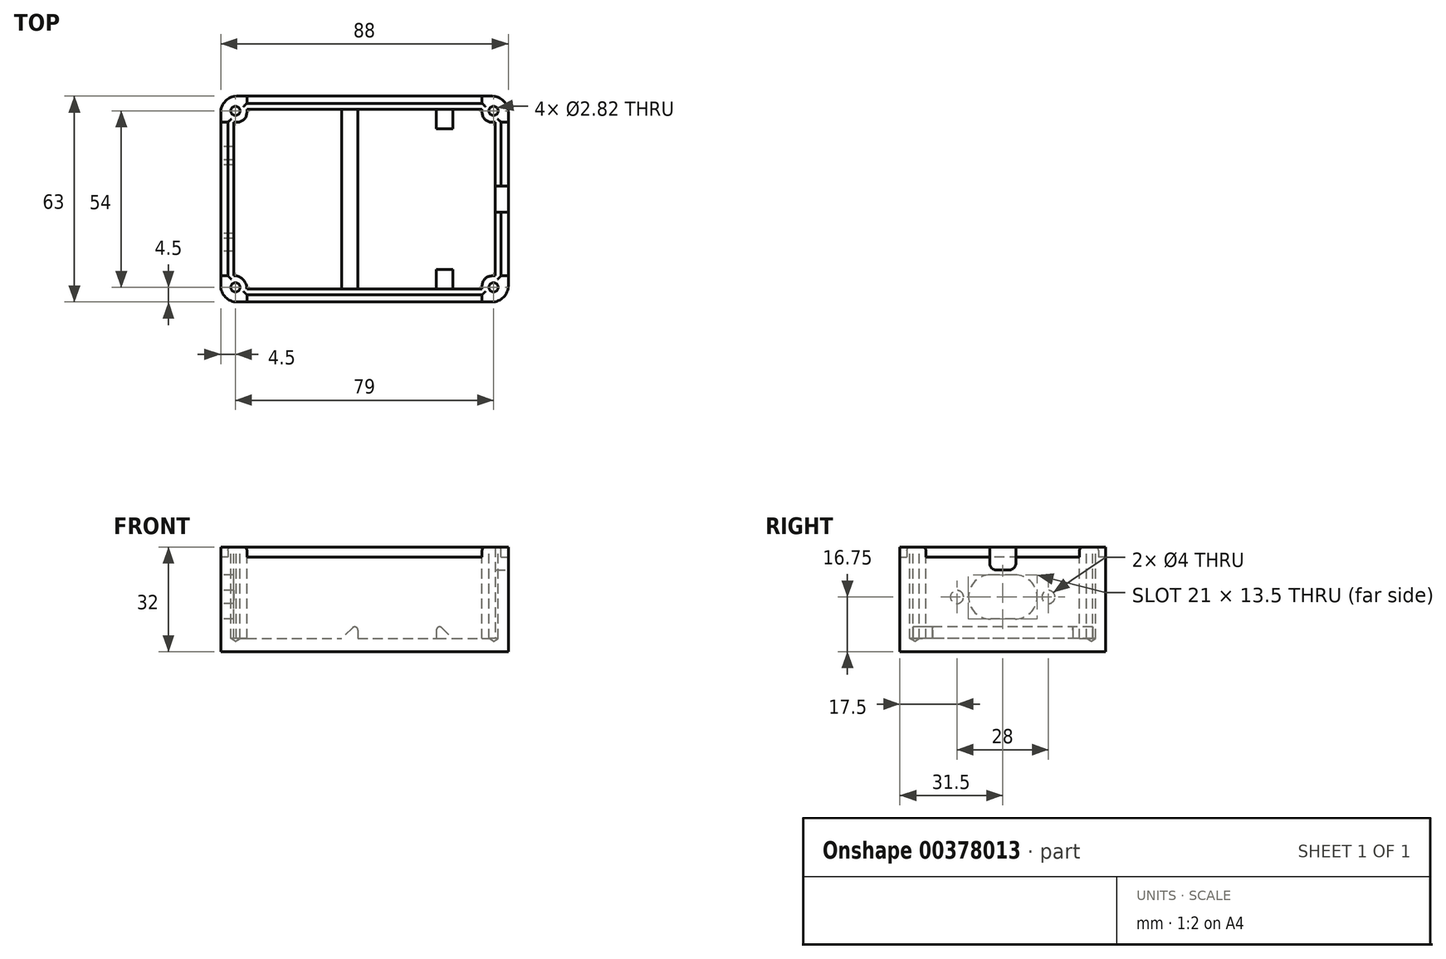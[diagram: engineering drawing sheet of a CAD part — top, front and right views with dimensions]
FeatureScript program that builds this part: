
annotation { "Feature Type Name" : "Feature", "Feature Type Description" : "" }
export const myFeature = defineFeature(function(context is Context, id is Id, definition is map)
    precondition{}
    {
        {
            var Q0;
            Q0=qCreatedBy(makeId("Top.planeOp"),FACE);
            cPlane(context, id + "F0", {"entities" : qUnion([Q0]), "cplaneType" : CPlaneType.OFFSET, "offset" : 25 * mm, "width" : 150 * mm, "height" : 150 * mm});
        }
        {
            var Q0;
            Q0=qCreatedBy(makeId("Top.planeOp"),FACE);
            var sketch = newSketch(context, id + "F1", { "sketchPlane" : qUnion([Q0])});
            skLineSegment(sketch, "E0.bottom", {"start": v(-80, 0) * mm, "end": v(0, 0) * mm});
            skLineSegment(sketch, "E0.top", {"start": v(-80, -55) * mm, "end": v(0, -55) * mm});
            skLineSegment(sketch, "E0.left", {"start": v(-80, 0) * mm, "end": v(-80, -55) * mm});
            skLineSegment(sketch, "E0.right", {"start": v(0, 0) * mm, "end": v(0, -55) * mm});
            skSolve(sketch);
        }
        {
            var Q0;
            Q0=makeQuery(id+"F1.imprint","IMPRINT",FACE,{"disambiguationData":[TD([[makeQuery(id+"F1.imprint","IMPRINT",EDGE,{"derivedFrom":sQuery(id+"F1.wireOp",EDGE,"E0.bottom")}),-1.0]])]});
            extrude(context, id + "F2", {"entities" : qUnion([Q0]), "depth" : 25 * mm});
        }
        {
            var Q0;
            Q0=makeQuery(id+"F2.opExtrude","CAP_FACE",FACE,{"disambiguationData":[OSD([sQuery(id+"F1.wireOp",EDGE,"E0.bottom"),sQuery(id+"F1.wireOp",EDGE,"E0.top"),sQuery(id+"F1.wireOp",EDGE,"E0.left"),sQuery(id+"F1.wireOp",EDGE,"E0.right")])],"isStart":false});
            shell(context, id + "F3", {"entities" : qUnion([Q0]), "thickness" : 4 * mm, "oppositeDirection" : true});
        }
        {
            var Q0;
            Q0=makeQuery(id+"F3.opShell","OFFSET_FACE",FACE,{"disambiguationData":[OSD([sQuery(id+"F1.wireOp",EDGE,"E0.bottom"),sQuery(id+"F1.wireOp",EDGE,"E0.top"),sQuery(id+"F1.wireOp",EDGE,"E0.left"),sQuery(id+"F1.wireOp",EDGE,"E0.right")])]});
            var sketch = newSketch(context, id + "F4", { "sketchPlane" : qUnion([Q0])});
            skLineSegment(sketch, "E1.bottom", {"start": v(-47, 0) * mm, "end": v(-42, 0) * mm});
            skLineSegment(sketch, "E1.top", {"start": v(-47, -55) * mm, "end": v(-42, -55) * mm});
            skLineSegment(sketch, "E1.left", {"start": v(-47, 0) * mm, "end": v(-47, -55) * mm});
            skLineSegment(sketch, "E1.right", {"start": v(-42, 0) * mm, "end": v(-42, -55) * mm});
            skSolve(sketch);
        }
        {
            var Q0;
            Q0 = qSketchRegion(id + "F4", true);
            extrude(context, id + "F5", {"entities" : qUnion([Q0]), "operationType" : NewBodyOperationType.ADD, "depth" : 5 * mm});
        }
        {
            var Q0;
            {var subQ0=sQuery(id+"F1.wireOp",EDGE,"E0.bottom");var subQ1=sQuery(id+"F1.wireOp",EDGE,"E0.top");var subQ2=sQuery(id+"F1.wireOp",EDGE,"E0.right");Q0=makeQuery(id+"F5.boolean.opBoolean","SPLIT",FACE,{"disambiguationData":[TD([makeQuery(id+"F3.opShell","OFFSET_FACE",FACE,{"disambiguationData":[OSD([subQ2])]})])],"derivedFrom":makeQuery(id+"F3.opShell","OFFSET_FACE",FACE,{"disambiguationData":[OSD([subQ0,subQ1,sQuery(id+"F1.wireOp",EDGE,"E0.left"),subQ2])]})});}
            var sketch = newSketch(context, id + "F6", { "sketchPlane" : qUnion([Q0])});
            skLineSegment(sketch, "E2.bottom", {"start": v(-18, 0) * mm, "end": v(-13, 0) * mm});
            skLineSegment(sketch, "E2.top", {"start": v(-18, -6) * mm, "end": v(-13, -6) * mm});
            skLineSegment(sketch, "E2.left", {"start": v(-18, 0) * mm, "end": v(-18, -6) * mm});
            skLineSegment(sketch, "E2.right", {"start": v(-13, 0) * mm, "end": v(-13, -6) * mm});
            skLineSegment(sketch, "E3.bottom", {"start": v(-18, -49) * mm, "end": v(-13, -49) * mm});
            skLineSegment(sketch, "E3.top", {"start": v(-18, -55) * mm, "end": v(-13, -55) * mm});
            skLineSegment(sketch, "E3.left", {"start": v(-18, -49) * mm, "end": v(-18, -55) * mm});
            skLineSegment(sketch, "E3.right", {"start": v(-13, -49) * mm, "end": v(-13, -55) * mm});
            skSolve(sketch);
        }
        {
            var Q0;
            Q0 = qSketchRegion(id + "F6", true);
            extrude(context, id + "F7", {"entities" : qUnion([Q0]), "operationType" : NewBodyOperationType.ADD, "depth" : 5 * mm});
        }
        {
            var Q0;
            Q0=qCreatedBy(id+"F0.planeOp",FACE);
            var sketch = newSketch(context, id + "F8", { "sketchPlane" : qUnion([Q0])});
            skLineSegment(sketch, "E4.bottom", {"start": v(-80, 0) * mm, "end": v(0, 0) * mm});
            skLineSegment(sketch, "E4.top", {"start": v(-80, -55) * mm, "end": v(0, -55) * mm});
            skLineSegment(sketch, "E4.left", {"start": v(-80, 0) * mm, "end": v(-80, -55) * mm});
            skLineSegment(sketch, "E4.right", {"start": v(0, 0) * mm, "end": v(0, -55) * mm});
            skLineSegment(sketch, "E5.bottom", {"start": v(-81.8, 1.8) * mm, "end": v(1.8, 1.8) * mm});
            skLineSegment(sketch, "E5.top", {"start": v(-81.8, -56.8) * mm, "end": v(1.8, -56.8) * mm});
            skLineSegment(sketch, "E5.left", {"start": v(-81.8, 1.8) * mm, "end": v(-81.8, -56.8) * mm});
            skLineSegment(sketch, "E5.right", {"start": v(1.8, 1.8) * mm, "end": v(1.8, -56.8) * mm});
            skSolve(sketch);
        }
        {
            var Q0;
            Q0 = qSketchRegion(id + "F8", true);
            extrude(context, id + "F9", {"entities" : qUnion([Q0]), "operationType" : NewBodyOperationType.ADD, "depth" : 3 * mm});
        }
        {
            var Q0;
            Q0=qCreatedBy(id+"F0.planeOp",FACE);
            var sketch = newSketch(context, id + "F10", { "sketchPlane" : qUnion([Q0])});
            skLineSegment(sketch, "E6", {"start": v(-79, -4) * mm, "end": v(-84, -4) * mm});
            skLineSegment(sketch, "E7", {"start": v(-84, -4) * mm, "end": v(-84, 4) * mm});
            skLineSegment(sketch, "E8", {"start": v(-84, 4) * mm, "end": v(-76, 4) * mm});
            skLineSegment(sketch, "E9", {"start": v(-76, 4) * mm, "end": v(-76, -1) * mm});
            skArc(sketch, "E10", {"start": v(-79, -4) * mm, "mid": v(-76.88, -3.12) * mm, "end": v(-76, -1) * mm});
            skLineSegment(sketch, "E11", {"start": v(-1, -4) * mm, "end": v(4, -4) * mm});
            skLineSegment(sketch, "E12", {"start": v(4, -4) * mm, "end": v(4, 4) * mm});
            skLineSegment(sketch, "E13", {"start": v(4, 4) * mm, "end": v(-4, 4) * mm});
            skLineSegment(sketch, "E14", {"start": v(-4, 4) * mm, "end": v(-4, -1) * mm});
            skLineSegment(sketch, "E15", {"start": v(-4, -54) * mm, "end": v(-4, -59) * mm});
            skLineSegment(sketch, "E16", {"start": v(-4, -59) * mm, "end": v(4, -59) * mm});
            skLineSegment(sketch, "E17", {"start": v(4, -59) * mm, "end": v(4, -51) * mm});
            skLineSegment(sketch, "E18", {"start": v(4, -51) * mm, "end": v(-1, -51) * mm});
            skArc(sketch, "E19", {"start": v(-1, -51) * mm, "mid": v(-3.12, -51.88) * mm, "end": v(-4, -54) * mm});
            skLineSegment(sketch, "E20", {"start": v(-79.19, -51) * mm, "end": v(-84, -51) * mm});
            skLineSegment(sketch, "E21", {"start": v(-84, -51) * mm, "end": v(-84, -59) * mm});
            skLineSegment(sketch, "E22", {"start": v(-84, -59) * mm, "end": v(-76, -59) * mm});
            skLineSegment(sketch, "E23", {"start": v(-76, -59) * mm, "end": v(-76, -55) * mm});
            skArc(sketch, "E24", {"start": v(-76, -55) * mm, "mid": v(-76.9, -52.44) * mm, "end": v(-79.19, -51) * mm});
            skArc(sketch, "E25", {"start": v(-4, -1) * mm, "mid": v(-3.12, -3.12) * mm, "end": v(-1, -4) * mm});
            skSolve(sketch);
        }
        {
            var Q0;
            Q0 = qSketchRegion(id + "F10", true);
            extrude(context, id + "F11", {"entities" : qUnion([Q0]), "operationType" : NewBodyOperationType.ADD, "oppositeDirection" : true, "depth" : 25 * mm});
        }
        {
            var Q0;
            Q0 = qSketchRegion(id + "F10", true);
            extrude(context, id + "F12", {"entities" : qUnion([Q0]), "operationType" : NewBodyOperationType.ADD, "depth" : 3 * mm});
        }
        {
            var Q0;
            Q0=makeQuery(id+"F12.boolean.opBoolean","MERGE",FACE,{"derivedFrom":[makeQuery(id+"F9.opExtrude","CAP_FACE",FACE,{"disambiguationData":[OSD([sQuery(id+"F8.wireOp",EDGE,"E4.bottom"),sQuery(id+"F8.wireOp",EDGE,"E4.top"),sQuery(id+"F8.wireOp",EDGE,"E4.left"),sQuery(id+"F8.wireOp",EDGE,"E4.right"),sQuery(id+"F8.wireOp",EDGE,"E5.bottom"),sQuery(id+"F8.wireOp",EDGE,"E5.top"),sQuery(id+"F8.wireOp",EDGE,"E5.left"),sQuery(id+"F8.wireOp",EDGE,"E5.right")])],"isStart":false}),makeQuery(id+"F12.opExtrude","CAP_FACE",FACE,{"disambiguationData":[OSD([sQuery(id+"F10.wireOp",EDGE,"E6"),sQuery(id+"F10.wireOp",EDGE,"E7"),sQuery(id+"F10.wireOp",EDGE,"E8"),sQuery(id+"F10.wireOp",EDGE,"E9"),sQuery(id+"F10.wireOp",EDGE,"E10")])],"isStart":false}),makeQuery(id+"F12.opExtrude","CAP_FACE",FACE,{"disambiguationData":[OSD([sQuery(id+"F10.wireOp",EDGE,"E11"),sQuery(id+"F10.wireOp",EDGE,"E12"),sQuery(id+"F10.wireOp",EDGE,"E13"),sQuery(id+"F10.wireOp",EDGE,"E14"),sQuery(id+"F10.wireOp",EDGE,"Bc1xN2n2-EDis-pzMm-qjfb-kigsFsctRrtZ")])],"isStart":false}),makeQuery(id+"F12.opExtrude","CAP_FACE",FACE,{"disambiguationData":[OSD([sQuery(id+"F10.wireOp",EDGE,"E15"),sQuery(id+"F10.wireOp",EDGE,"E16"),sQuery(id+"F10.wireOp",EDGE,"E17"),sQuery(id+"F10.wireOp",EDGE,"E18"),sQuery(id+"F10.wireOp",EDGE,"E19")])],"isStart":false}),makeQuery(id+"F12.opExtrude","CAP_FACE",FACE,{"disambiguationData":[OSD([sQuery(id+"F10.wireOp",EDGE,"E20"),sQuery(id+"F10.wireOp",EDGE,"E21"),sQuery(id+"F10.wireOp",EDGE,"E22"),sQuery(id+"F10.wireOp",EDGE,"E23"),sQuery(id+"F10.wireOp",EDGE,"E24")])],"isStart":false})]});
            var sketch = newSketch(context, id + "F13", { "sketchPlane" : qUnion([Q0])});
            skPoint(sketch, "E26", {"position": v(-79.5, -0.5) * mm});
            skPoint(sketch, "E27", {"position": v(-0.5, -0.5) * mm});
            skPoint(sketch, "E28", {"position": v(-0.5, -54.5) * mm});
            skPoint(sketch, "E29", {"position": v(-79.5, -54.5) * mm});
            skSolve(sketch);
        }
        {
            var Q0;
            Q0=sQuery(id+"F13.wireOp",VERTEX,"E26");
            var Q1;
            Q1=sQuery(id+"F13.wireOp",VERTEX,"E27");
            var Q2;
            Q2=sQuery(id+"F13.wireOp",VERTEX,"E28");
            var Q3;
            Q3=sQuery(id+"F13.wireOp",VERTEX,"E29");
            var Q4;
            Q4=makeQuery(id+"F2.opExtrude","SWEPT_BODY",BODY,{"disambiguationData":[OSD([sQuery(id+"F1.wireOp",EDGE,"E0.bottom"),sQuery(id+"F1.wireOp",EDGE,"E0.top"),sQuery(id+"F1.wireOp",EDGE,"E0.left"),sQuery(id+"F1.wireOp",EDGE,"E0.right")])]});
            hole(context, id + "F14", {"style" : HoleStyle.SIMPLE, "endStyle" : HoleEndStyle.BLIND, "holeDiameter" : 2.82 * mm, "holeDepth" : 28 * mm, "tappedDepth" : 12 * mm, "tapClearance" : 3, "locations" : qUnion([Q0, Q1, Q2, Q3]), "scope" : qUnion([Q4])});
        }
        {
            var Q0;
            Q0=makeQuery(id+"F12.boolean.opBoolean","MERGE",FACE,{"derivedFrom":[makeQuery(id+"F2.opExtrude","SWEPT_FACE",FACE,{"disambiguationData":[OSD([sQuery(id+"F1.wireOp",EDGE,"E0.right")])]}),makeQuery(id+"F12.opExtrude","SWEPT_FACE",FACE,{"disambiguationData":[OSD([sQuery(id+"F10.wireOp",EDGE,"E12")])]}),makeQuery(id+"F12.opExtrude","SWEPT_FACE",FACE,{"disambiguationData":[OSD([sQuery(id+"F10.wireOp",EDGE,"E17")])]})]});
            var sketch = newSketch(context, id + "F15", { "sketchPlane" : qUnion([Q0])});
            skLineSegment(sketch, "E30.bottom", {"start": v(-31.5, 28) * mm, "end": v(-23.5, 28) * mm});
            skLineSegment(sketch, "E30.top", {"start": v(-31.5, 21) * mm, "end": v(-23.5, 21) * mm});
            skLineSegment(sketch, "E30.left", {"start": v(-31.5, 28) * mm, "end": v(-31.5, 21) * mm});
            skLineSegment(sketch, "E30.right", {"start": v(-23.5, 28) * mm, "end": v(-23.5, 21) * mm});
            skSolve(sketch);
        }
        {
            var Q0;
            Q0 = qSketchRegion(id + "F15", true);
            extrude(context, id + "F16", {"entities" : qUnion([Q0]), "operationType" : NewBodyOperationType.REMOVE, "oppositeDirection" : true, "depth" : 4 * mm});
        }
        {
            var Q0;
            Q0=makeQuery(id+"F12.boolean.opBoolean","MERGE",FACE,{"derivedFrom":[makeQuery(id+"F2.opExtrude","SWEPT_FACE",FACE,{"disambiguationData":[OSD([sQuery(id+"F1.wireOp",EDGE,"E0.left")])]}),makeQuery(id+"F12.opExtrude","SWEPT_FACE",FACE,{"disambiguationData":[OSD([sQuery(id+"F10.wireOp",EDGE,"E7")])]}),makeQuery(id+"F12.opExtrude","SWEPT_FACE",FACE,{"disambiguationData":[OSD([sQuery(id+"F10.wireOp",EDGE,"E21")])]})]});
            var sketch = newSketch(context, id + "F17", { "sketchPlane" : qUnion([Q0])});
            skLineSegment(sketch, "E31.bottom", {"start": v(23.75, 19.5) * mm, "end": v(31.25, 19.5) * mm});
            skLineSegment(sketch, "E31.top", {"start": v(23.75, 6) * mm, "end": v(31.25, 6) * mm});
            skLineSegment(sketch, "E31.left", {"start": v(17, 12.75) * mm, "end": v(17, 12.75) * mm});
            skLineSegment(sketch, "E31.right", {"start": v(38, 12.75) * mm, "end": v(38, 12.75) * mm});
            skPoint(sketch, "E32.visualSharp", {"position": v(17, 19.5) * mm});
            skArc(sketch, "E32.filletArc", {"start": v(23.75, 19.5) * mm, "mid": v(18.98, 17.52) * mm, "end": v(17, 12.75) * mm});
            skPoint(sketch, "E33.visualSharp", {"position": v(17, 6) * mm});
            skArc(sketch, "E33.filletArc", {"start": v(17, 12.75) * mm, "mid": v(18.98, 7.98) * mm, "end": v(23.75, 6) * mm});
            skPoint(sketch, "E34.visualSharp", {"position": v(38, 6) * mm});
            skArc(sketch, "E34.filletArc", {"start": v(31.25, 6) * mm, "mid": v(36.02, 7.98) * mm, "end": v(38, 12.75) * mm});
            skPoint(sketch, "E35.visualSharp", {"position": v(38, 19.5) * mm});
            skArc(sketch, "E35.filletArc", {"start": v(38, 12.75) * mm, "mid": v(36.02, 17.52) * mm, "end": v(31.25, 19.5) * mm});
            skSolve(sketch);
        }
        {
            var Q0;
            Q0=makeQuery(id+"F12.boolean.opBoolean","MERGE",FACE,{"derivedFrom":[makeQuery(id+"F2.opExtrude","SWEPT_FACE",FACE,{"disambiguationData":[OSD([sQuery(id+"F1.wireOp",EDGE,"E0.left")])]}),makeQuery(id+"F12.opExtrude","SWEPT_FACE",FACE,{"disambiguationData":[OSD([sQuery(id+"F10.wireOp",EDGE,"E7")])]}),makeQuery(id+"F12.opExtrude","SWEPT_FACE",FACE,{"disambiguationData":[OSD([sQuery(id+"F10.wireOp",EDGE,"E21")])]})]});
            var sketch = newSketch(context, id + "F18", { "sketchPlane" : qUnion([Q0])});
            skPoint(sketch, "E36", {"position": v(13.5, 12.75) * mm});
            skPoint(sketch, "E37", {"position": v(41.5, 12.75) * mm});
            skSolve(sketch);
        }
        {
            var Q0;
            Q0 = qSketchRegion(id + "F17", true);
            extrude(context, id + "F19", {"entities" : qUnion([Q0]), "operationType" : NewBodyOperationType.REMOVE, "oppositeDirection" : true, "depth" : 4 * mm});
        }
        {
            var Q0;
            Q0=sQuery(id+"F18.wireOp",VERTEX,"E36");
            var Q1;
            Q1=sQuery(id+"F18.wireOp",VERTEX,"E37");
            var Q2;
            Q2=makeQuery(id+"F2.opExtrude","SWEPT_BODY",BODY,{"disambiguationData":[OSD([sQuery(id+"F1.wireOp",EDGE,"E0.bottom"),sQuery(id+"F1.wireOp",EDGE,"E0.top"),sQuery(id+"F1.wireOp",EDGE,"E0.left"),sQuery(id+"F1.wireOp",EDGE,"E0.right")])]});
            hole(context, id + "F20", {"style" : HoleStyle.SIMPLE, "endStyle" : HoleEndStyle.BLIND, "holeDiameter" : 4 * mm, "holeDepth" : 4 * mm, "tappedDepth" : 12 * mm, "tapClearance" : 3, "locations" : qUnion([Q0, Q1]), "scope" : qUnion([Q2])});
        }
        {
            var Q0;
            Q0=makeQuery(id+"F5.opExtrude","CAP_EDGE",EDGE,{"disambiguationData":[OSD([sQuery(id+"F4.wireOp",EDGE,"E1.left")])],"isStart":false});
            var Q1;
            Q1=makeQuery(id+"F7.opExtrude","CAP_EDGE",EDGE,{"disambiguationData":[OSD([sQuery(id+"F6.wireOp",EDGE,"E2.right")])],"isStart":false});
            var Q2;
            Q2=makeQuery(id+"F7.opExtrude","CAP_EDGE",EDGE,{"disambiguationData":[OSD([sQuery(id+"F6.wireOp",EDGE,"E3.right")])],"isStart":false});
            chamfer(context, id + "F21", {"entities" : qUnion([Q0, Q1, Q2]), "width" : 5 * mm, "tangentPropagation" : true});
        }
        {
            var Q0;
            Q0=makeQuery(id+"F12.boolean.opBoolean","MERGE",EDGE,{"derivedFrom":[makeQuery(id+"F2.opExtrude","SWEPT_EDGE",EDGE,{"disambiguationData":[OSD([sQuery(id+"F1.wireOp",EDGE,"E0.bottom"),sQuery(id+"F1.wireOp",EDGE,"E0.left")])]}),makeQuery(id+"F12.opExtrude","SWEPT_EDGE",EDGE,{"disambiguationData":[OSD([sQuery(id+"F10.wireOp",EDGE,"E7"),sQuery(id+"F10.wireOp",EDGE,"E8")])]})]});
            var Q1;
            Q1=makeQuery(id+"F12.boolean.opBoolean","MERGE",EDGE,{"derivedFrom":[makeQuery(id+"F2.opExtrude","SWEPT_EDGE",EDGE,{"disambiguationData":[OSD([sQuery(id+"F1.wireOp",EDGE,"E0.top"),sQuery(id+"F1.wireOp",EDGE,"E0.left")])]}),makeQuery(id+"F12.opExtrude","SWEPT_EDGE",EDGE,{"disambiguationData":[OSD([sQuery(id+"F10.wireOp",EDGE,"E21"),sQuery(id+"F10.wireOp",EDGE,"E22")])]})]});
            var Q2;
            Q2=makeQuery(id+"F12.boolean.opBoolean","MERGE",EDGE,{"derivedFrom":[makeQuery(id+"F2.opExtrude","SWEPT_EDGE",EDGE,{"disambiguationData":[OSD([sQuery(id+"F1.wireOp",EDGE,"E0.top"),sQuery(id+"F1.wireOp",EDGE,"E0.right")])]}),makeQuery(id+"F12.opExtrude","SWEPT_EDGE",EDGE,{"disambiguationData":[OSD([sQuery(id+"F10.wireOp",EDGE,"E16"),sQuery(id+"F10.wireOp",EDGE,"E17")])]})]});
            var Q3;
            Q3=makeQuery(id+"F12.boolean.opBoolean","MERGE",EDGE,{"derivedFrom":[makeQuery(id+"F2.opExtrude","SWEPT_EDGE",EDGE,{"disambiguationData":[OSD([sQuery(id+"F1.wireOp",EDGE,"E0.bottom"),sQuery(id+"F1.wireOp",EDGE,"E0.right")])]}),makeQuery(id+"F12.opExtrude","SWEPT_EDGE",EDGE,{"disambiguationData":[OSD([sQuery(id+"F10.wireOp",EDGE,"E12"),sQuery(id+"F10.wireOp",EDGE,"E13")])]})]});
            fillet(context, id + "F22", {"entities" : qUnion([Q0, Q1, Q2, Q3]), "radius" : 5 * mm, "tangentPropagation" : true, "allowEdgeOverflow" : false});
        }
        {
            var Q0;
            Q0=makeQuery(id+"F16.boolean.opBoolean","COPY",EDGE,{"derivedFrom":makeQuery(id+"F16.opExtrude","SWEPT_EDGE",EDGE,{"disambiguationData":[OSD([sQuery(id+"F15.wireOp",EDGE,"E30.top"),sQuery(id+"F15.wireOp",EDGE,"E30.left")])]})});
            var Q1;
            Q1=makeQuery(id+"F16.boolean.opBoolean","COPY",EDGE,{"derivedFrom":makeQuery(id+"F16.opExtrude","SWEPT_EDGE",EDGE,{"disambiguationData":[OSD([sQuery(id+"F15.wireOp",EDGE,"E30.top"),sQuery(id+"F15.wireOp",EDGE,"E30.right")])]})});
            fillet(context, id + "F23", {"entities" : qUnion([Q0, Q1]), "radius" : 2 * mm, "tangentPropagation" : true, "allowEdgeOverflow" : false});
        }
        {
            var Q0;
            Q0=makeQuery(id+"F9.opExtrude","CAP_EDGE",EDGE,{"disambiguationData":[OSD([sQuery(id+"F8.wireOp",EDGE,"E5.top")])],"isStart":false});
            var Q1;
            {var subQ0=sQuery(id+"F8.wireOp",EDGE,"E5.right");var subQ1=sQuery(id+"F10.wireOp",EDGE,"E18");Q1=makeQuery(id+"F16.boolean.opBoolean","SPLIT",EDGE,{"disambiguationData":[TD([makeQuery(id+"F12.opExtrude","SWEPT_FACE",FACE,{"disambiguationData":[OSD([subQ1])]})])],"derivedFrom":makeQuery(id+"F9.opExtrude","CAP_EDGE",EDGE,{"disambiguationData":[OSD([subQ0])],"isStart":false})});}
            var Q2;
            {var subQ0=sQuery(id+"F10.wireOp",EDGE,"E11");var subQ1=sQuery(id+"F8.wireOp",EDGE,"E5.right");Q2=makeQuery(id+"F16.boolean.opBoolean","SPLIT",EDGE,{"disambiguationData":[TD([makeQuery(id+"F12.opExtrude","SWEPT_FACE",FACE,{"disambiguationData":[OSD([subQ0])]})])],"derivedFrom":makeQuery(id+"F9.opExtrude","CAP_EDGE",EDGE,{"disambiguationData":[OSD([subQ1])],"isStart":false})});}
            var Q3;
            Q3=makeQuery(id+"F9.opExtrude","CAP_EDGE",EDGE,{"disambiguationData":[OSD([sQuery(id+"F8.wireOp",EDGE,"E5.bottom")])],"isStart":false});
            var Q4;
            Q4=makeQuery(id+"F9.opExtrude","CAP_EDGE",EDGE,{"disambiguationData":[OSD([sQuery(id+"F8.wireOp",EDGE,"E5.left")])],"isStart":false});
            var Q5;
            Q5=makeQuery(id+"F12.opExtrude","CAP_EDGE",EDGE,{"disambiguationData":[OSD([sQuery(id+"F10.wireOp",EDGE,"E23")])],"isStart":false});
            var Q6;
            {var subQ0=sQuery(id+"F10.wireOp",EDGE,"E20");Q6=makeQuery(id+"F12.boolean.opBoolean","SPLIT",EDGE,{"disambiguationData":[topologyDisambiguationEdgeConnected([makeQuery(id+"F9.opExtrude","CAP_FACE",FACE,{"disambiguationData":[OSD([sQuery(id+"F8.wireOp",EDGE,"E4.bottom"),sQuery(id+"F8.wireOp",EDGE,"E4.top"),sQuery(id+"F8.wireOp",EDGE,"E4.left"),sQuery(id+"F8.wireOp",EDGE,"E4.right"),sQuery(id+"F8.wireOp",EDGE,"E5.bottom"),sQuery(id+"F8.wireOp",EDGE,"E5.top"),sQuery(id+"F8.wireOp",EDGE,"E5.left"),sQuery(id+"F8.wireOp",EDGE,"E5.right")])],"isStart":false}),makeQuery(id+"F12.opExtrude","CAP_FACE",FACE,{"disambiguationData":[OSD([sQuery(id+"F10.wireOp",EDGE,"E6"),sQuery(id+"F10.wireOp",EDGE,"E7"),sQuery(id+"F10.wireOp",EDGE,"E8"),sQuery(id+"F10.wireOp",EDGE,"E9"),sQuery(id+"F10.wireOp",EDGE,"E10")])],"isStart":false}),makeQuery(id+"F12.opExtrude","CAP_FACE",FACE,{"disambiguationData":[OSD([sQuery(id+"F10.wireOp",EDGE,"E11"),sQuery(id+"F10.wireOp",EDGE,"E12"),sQuery(id+"F10.wireOp",EDGE,"E13"),sQuery(id+"F10.wireOp",EDGE,"E14"),sQuery(id+"F10.wireOp",EDGE,"E25")])],"isStart":false}),makeQuery(id+"F12.opExtrude","CAP_FACE",FACE,{"disambiguationData":[OSD([sQuery(id+"F10.wireOp",EDGE,"E15"),sQuery(id+"F10.wireOp",EDGE,"E16"),sQuery(id+"F10.wireOp",EDGE,"E17"),sQuery(id+"F10.wireOp",EDGE,"E18"),sQuery(id+"F10.wireOp",EDGE,"E19")])],"isStart":false}),makeQuery(id+"F12.opExtrude","SWEPT_FACE",FACE,{"disambiguationData":[OSD([subQ0])]}),makeQuery(id+"F12.opExtrude","CAP_FACE",FACE,{"disambiguationData":[OSD([subQ0,sQuery(id+"F10.wireOp",EDGE,"E21"),sQuery(id+"F10.wireOp",EDGE,"E22"),sQuery(id+"F10.wireOp",EDGE,"E23"),sQuery(id+"F10.wireOp",EDGE,"E24")])],"isStart":false})])],"derivedFrom":makeQuery(id+"F12.opExtrude","CAP_EDGE",EDGE,{"disambiguationData":[OSD([subQ0])],"isStart":false})});}
            var Q7;
            {var subQ0=sQuery(id+"F10.wireOp",EDGE,"E6");Q7=makeQuery(id+"F12.boolean.opBoolean","SPLIT",EDGE,{"disambiguationData":[topologyDisambiguationEdgeConnected([makeQuery(id+"F9.opExtrude","CAP_FACE",FACE,{"disambiguationData":[OSD([sQuery(id+"F8.wireOp",EDGE,"E4.bottom"),sQuery(id+"F8.wireOp",EDGE,"E4.top"),sQuery(id+"F8.wireOp",EDGE,"E4.left"),sQuery(id+"F8.wireOp",EDGE,"E4.right"),sQuery(id+"F8.wireOp",EDGE,"E5.bottom"),sQuery(id+"F8.wireOp",EDGE,"E5.top"),sQuery(id+"F8.wireOp",EDGE,"E5.left"),sQuery(id+"F8.wireOp",EDGE,"E5.right")])],"isStart":false}),makeQuery(id+"F12.opExtrude","SWEPT_FACE",FACE,{"disambiguationData":[OSD([subQ0])]}),makeQuery(id+"F12.opExtrude","CAP_FACE",FACE,{"disambiguationData":[OSD([subQ0,sQuery(id+"F10.wireOp",EDGE,"E7"),sQuery(id+"F10.wireOp",EDGE,"E8"),sQuery(id+"F10.wireOp",EDGE,"E9"),sQuery(id+"F10.wireOp",EDGE,"E10")])],"isStart":false}),makeQuery(id+"F12.opExtrude","CAP_FACE",FACE,{"disambiguationData":[OSD([sQuery(id+"F10.wireOp",EDGE,"E11"),sQuery(id+"F10.wireOp",EDGE,"E12"),sQuery(id+"F10.wireOp",EDGE,"E13"),sQuery(id+"F10.wireOp",EDGE,"E14"),sQuery(id+"F10.wireOp",EDGE,"E25")])],"isStart":false}),makeQuery(id+"F12.opExtrude","CAP_FACE",FACE,{"disambiguationData":[OSD([sQuery(id+"F10.wireOp",EDGE,"E15"),sQuery(id+"F10.wireOp",EDGE,"E16"),sQuery(id+"F10.wireOp",EDGE,"E17"),sQuery(id+"F10.wireOp",EDGE,"E18"),sQuery(id+"F10.wireOp",EDGE,"E19")])],"isStart":false}),makeQuery(id+"F12.opExtrude","CAP_FACE",FACE,{"disambiguationData":[OSD([sQuery(id+"F10.wireOp",EDGE,"E20"),sQuery(id+"F10.wireOp",EDGE,"E21"),sQuery(id+"F10.wireOp",EDGE,"E22"),sQuery(id+"F10.wireOp",EDGE,"E23"),sQuery(id+"F10.wireOp",EDGE,"E24")])],"isStart":false})])],"derivedFrom":makeQuery(id+"F12.opExtrude","CAP_EDGE",EDGE,{"disambiguationData":[OSD([subQ0])],"isStart":false})});}
            var Q8;
            {var subQ0=sQuery(id+"F10.wireOp",EDGE,"E9");Q8=makeQuery(id+"F12.boolean.opBoolean","SPLIT",EDGE,{"disambiguationData":[topologyDisambiguationEdgeConnected([makeQuery(id+"F9.opExtrude","CAP_FACE",FACE,{"disambiguationData":[OSD([sQuery(id+"F8.wireOp",EDGE,"E4.bottom"),sQuery(id+"F8.wireOp",EDGE,"E4.top"),sQuery(id+"F8.wireOp",EDGE,"E4.left"),sQuery(id+"F8.wireOp",EDGE,"E4.right"),sQuery(id+"F8.wireOp",EDGE,"E5.bottom"),sQuery(id+"F8.wireOp",EDGE,"E5.top"),sQuery(id+"F8.wireOp",EDGE,"E5.left"),sQuery(id+"F8.wireOp",EDGE,"E5.right")])],"isStart":false}),makeQuery(id+"F12.opExtrude","CAP_FACE",FACE,{"disambiguationData":[OSD([sQuery(id+"F10.wireOp",EDGE,"E6"),sQuery(id+"F10.wireOp",EDGE,"E7"),sQuery(id+"F10.wireOp",EDGE,"E8"),subQ0,sQuery(id+"F10.wireOp",EDGE,"E10")])],"isStart":false}),makeQuery(id+"F12.opExtrude","SWEPT_FACE",FACE,{"disambiguationData":[OSD([subQ0])]}),makeQuery(id+"F12.opExtrude","CAP_FACE",FACE,{"disambiguationData":[OSD([sQuery(id+"F10.wireOp",EDGE,"E11"),sQuery(id+"F10.wireOp",EDGE,"E12"),sQuery(id+"F10.wireOp",EDGE,"E13"),sQuery(id+"F10.wireOp",EDGE,"E14"),sQuery(id+"F10.wireOp",EDGE,"E25")])],"isStart":false}),makeQuery(id+"F12.opExtrude","CAP_FACE",FACE,{"disambiguationData":[OSD([sQuery(id+"F10.wireOp",EDGE,"E15"),sQuery(id+"F10.wireOp",EDGE,"E16"),sQuery(id+"F10.wireOp",EDGE,"E17"),sQuery(id+"F10.wireOp",EDGE,"E18"),sQuery(id+"F10.wireOp",EDGE,"E19")])],"isStart":false}),makeQuery(id+"F12.opExtrude","CAP_FACE",FACE,{"disambiguationData":[OSD([sQuery(id+"F10.wireOp",EDGE,"E20"),sQuery(id+"F10.wireOp",EDGE,"E21"),sQuery(id+"F10.wireOp",EDGE,"E22"),sQuery(id+"F10.wireOp",EDGE,"E23"),sQuery(id+"F10.wireOp",EDGE,"E24")])],"isStart":false})])],"derivedFrom":makeQuery(id+"F12.opExtrude","CAP_EDGE",EDGE,{"disambiguationData":[OSD([subQ0])],"isStart":false})});}
            var Q9;
            {var subQ0=sQuery(id+"F10.wireOp",EDGE,"E14");Q9=makeQuery(id+"F12.boolean.opBoolean","SPLIT",EDGE,{"disambiguationData":[topologyDisambiguationEdgeConnected([makeQuery(id+"F9.opExtrude","CAP_FACE",FACE,{"disambiguationData":[OSD([sQuery(id+"F8.wireOp",EDGE,"E4.bottom"),sQuery(id+"F8.wireOp",EDGE,"E4.top"),sQuery(id+"F8.wireOp",EDGE,"E4.left"),sQuery(id+"F8.wireOp",EDGE,"E4.right"),sQuery(id+"F8.wireOp",EDGE,"E5.bottom"),sQuery(id+"F8.wireOp",EDGE,"E5.top"),sQuery(id+"F8.wireOp",EDGE,"E5.left"),sQuery(id+"F8.wireOp",EDGE,"E5.right")])],"isStart":false}),makeQuery(id+"F12.opExtrude","CAP_FACE",FACE,{"disambiguationData":[OSD([sQuery(id+"F10.wireOp",EDGE,"E6"),sQuery(id+"F10.wireOp",EDGE,"E7"),sQuery(id+"F10.wireOp",EDGE,"E8"),sQuery(id+"F10.wireOp",EDGE,"E9"),sQuery(id+"F10.wireOp",EDGE,"E10")])],"isStart":false}),makeQuery(id+"F12.opExtrude","CAP_FACE",FACE,{"disambiguationData":[OSD([sQuery(id+"F10.wireOp",EDGE,"E11"),sQuery(id+"F10.wireOp",EDGE,"E12"),sQuery(id+"F10.wireOp",EDGE,"E13"),subQ0,sQuery(id+"F10.wireOp",EDGE,"E25")])],"isStart":false}),makeQuery(id+"F12.opExtrude","SWEPT_FACE",FACE,{"disambiguationData":[OSD([subQ0])]}),makeQuery(id+"F12.opExtrude","CAP_FACE",FACE,{"disambiguationData":[OSD([sQuery(id+"F10.wireOp",EDGE,"E15"),sQuery(id+"F10.wireOp",EDGE,"E16"),sQuery(id+"F10.wireOp",EDGE,"E17"),sQuery(id+"F10.wireOp",EDGE,"E18"),sQuery(id+"F10.wireOp",EDGE,"E19")])],"isStart":false}),makeQuery(id+"F12.opExtrude","CAP_FACE",FACE,{"disambiguationData":[OSD([sQuery(id+"F10.wireOp",EDGE,"E20"),sQuery(id+"F10.wireOp",EDGE,"E21"),sQuery(id+"F10.wireOp",EDGE,"E22"),sQuery(id+"F10.wireOp",EDGE,"E23"),sQuery(id+"F10.wireOp",EDGE,"E24")])],"isStart":false})])],"derivedFrom":makeQuery(id+"F12.opExtrude","CAP_EDGE",EDGE,{"disambiguationData":[OSD([subQ0])],"isStart":false})});}
            var Q10;
            {var subQ0=sQuery(id+"F10.wireOp",EDGE,"E11");Q10=makeQuery(id+"F12.boolean.opBoolean","SPLIT",EDGE,{"disambiguationData":[topologyDisambiguationEdgeConnected([makeQuery(id+"F9.opExtrude","CAP_FACE",FACE,{"disambiguationData":[OSD([sQuery(id+"F8.wireOp",EDGE,"E4.bottom"),sQuery(id+"F8.wireOp",EDGE,"E4.top"),sQuery(id+"F8.wireOp",EDGE,"E4.left"),sQuery(id+"F8.wireOp",EDGE,"E4.right"),sQuery(id+"F8.wireOp",EDGE,"E5.bottom"),sQuery(id+"F8.wireOp",EDGE,"E5.top"),sQuery(id+"F8.wireOp",EDGE,"E5.left"),sQuery(id+"F8.wireOp",EDGE,"E5.right")])],"isStart":false}),makeQuery(id+"F12.opExtrude","CAP_FACE",FACE,{"disambiguationData":[OSD([sQuery(id+"F10.wireOp",EDGE,"E6"),sQuery(id+"F10.wireOp",EDGE,"E7"),sQuery(id+"F10.wireOp",EDGE,"E8"),sQuery(id+"F10.wireOp",EDGE,"E9"),sQuery(id+"F10.wireOp",EDGE,"E10")])],"isStart":false}),makeQuery(id+"F12.opExtrude","SWEPT_FACE",FACE,{"disambiguationData":[OSD([subQ0])]}),makeQuery(id+"F12.opExtrude","CAP_FACE",FACE,{"disambiguationData":[OSD([subQ0,sQuery(id+"F10.wireOp",EDGE,"E12"),sQuery(id+"F10.wireOp",EDGE,"E13"),sQuery(id+"F10.wireOp",EDGE,"E14"),sQuery(id+"F10.wireOp",EDGE,"E25")])],"isStart":false}),makeQuery(id+"F12.opExtrude","CAP_FACE",FACE,{"disambiguationData":[OSD([sQuery(id+"F10.wireOp",EDGE,"E15"),sQuery(id+"F10.wireOp",EDGE,"E16"),sQuery(id+"F10.wireOp",EDGE,"E17"),sQuery(id+"F10.wireOp",EDGE,"E18"),sQuery(id+"F10.wireOp",EDGE,"E19")])],"isStart":false}),makeQuery(id+"F12.opExtrude","CAP_FACE",FACE,{"disambiguationData":[OSD([sQuery(id+"F10.wireOp",EDGE,"E20"),sQuery(id+"F10.wireOp",EDGE,"E21"),sQuery(id+"F10.wireOp",EDGE,"E22"),sQuery(id+"F10.wireOp",EDGE,"E23"),sQuery(id+"F10.wireOp",EDGE,"E24")])],"isStart":false})])],"derivedFrom":makeQuery(id+"F12.opExtrude","CAP_EDGE",EDGE,{"disambiguationData":[OSD([subQ0])],"isStart":false})});}
            var Q11;
            Q11=makeQuery(id+"F16.boolean.opBoolean","COPY",EDGE,{"derivedFrom":makeQuery(id+"F16.opExtrude","SWEPT_EDGE",EDGE,{"disambiguationData":[OSD([sQuery(id+"F15.wireOp",EDGE,"E30.bottom"),sQuery(id+"F15.wireOp",EDGE,"E30.left")])]})});
            var Q12;
            Q12=makeQuery(id+"F16.boolean.opBoolean","COPY",EDGE,{"derivedFrom":makeQuery(id+"F16.opExtrude","SWEPT_EDGE",EDGE,{"disambiguationData":[OSD([sQuery(id+"F15.wireOp",EDGE,"E30.bottom"),sQuery(id+"F15.wireOp",EDGE,"E30.right")])]})});
            var Q13;
            {var subQ0=sQuery(id+"F10.wireOp",EDGE,"E18");Q13=makeQuery(id+"F12.boolean.opBoolean","SPLIT",EDGE,{"disambiguationData":[topologyDisambiguationEdgeConnected([makeQuery(id+"F9.opExtrude","CAP_FACE",FACE,{"disambiguationData":[OSD([sQuery(id+"F8.wireOp",EDGE,"E4.bottom"),sQuery(id+"F8.wireOp",EDGE,"E4.top"),sQuery(id+"F8.wireOp",EDGE,"E4.left"),sQuery(id+"F8.wireOp",EDGE,"E4.right"),sQuery(id+"F8.wireOp",EDGE,"E5.bottom"),sQuery(id+"F8.wireOp",EDGE,"E5.top"),sQuery(id+"F8.wireOp",EDGE,"E5.left"),sQuery(id+"F8.wireOp",EDGE,"E5.right")])],"isStart":false}),makeQuery(id+"F12.opExtrude","CAP_FACE",FACE,{"disambiguationData":[OSD([sQuery(id+"F10.wireOp",EDGE,"E6"),sQuery(id+"F10.wireOp",EDGE,"E7"),sQuery(id+"F10.wireOp",EDGE,"E8"),sQuery(id+"F10.wireOp",EDGE,"E9"),sQuery(id+"F10.wireOp",EDGE,"E10")])],"isStart":false}),makeQuery(id+"F12.opExtrude","CAP_FACE",FACE,{"disambiguationData":[OSD([sQuery(id+"F10.wireOp",EDGE,"E11"),sQuery(id+"F10.wireOp",EDGE,"E12"),sQuery(id+"F10.wireOp",EDGE,"E13"),sQuery(id+"F10.wireOp",EDGE,"E14"),sQuery(id+"F10.wireOp",EDGE,"E25")])],"isStart":false}),makeQuery(id+"F12.opExtrude","CAP_FACE",FACE,{"disambiguationData":[OSD([sQuery(id+"F10.wireOp",EDGE,"E15"),sQuery(id+"F10.wireOp",EDGE,"E16"),sQuery(id+"F10.wireOp",EDGE,"E17"),subQ0,sQuery(id+"F10.wireOp",EDGE,"E19")])],"isStart":false}),makeQuery(id+"F12.opExtrude","SWEPT_FACE",FACE,{"disambiguationData":[OSD([subQ0])]}),makeQuery(id+"F12.opExtrude","CAP_FACE",FACE,{"disambiguationData":[OSD([sQuery(id+"F10.wireOp",EDGE,"E20"),sQuery(id+"F10.wireOp",EDGE,"E21"),sQuery(id+"F10.wireOp",EDGE,"E22"),sQuery(id+"F10.wireOp",EDGE,"E23"),sQuery(id+"F10.wireOp",EDGE,"E24")])],"isStart":false})])],"derivedFrom":makeQuery(id+"F12.opExtrude","CAP_EDGE",EDGE,{"disambiguationData":[OSD([subQ0])],"isStart":false})});}
            var Q14;
            {var subQ0=sQuery(id+"F10.wireOp",EDGE,"E15");Q14=makeQuery(id+"F12.boolean.opBoolean","SPLIT",EDGE,{"disambiguationData":[topologyDisambiguationEdgeConnected([makeQuery(id+"F9.opExtrude","CAP_FACE",FACE,{"disambiguationData":[OSD([sQuery(id+"F8.wireOp",EDGE,"E4.bottom"),sQuery(id+"F8.wireOp",EDGE,"E4.top"),sQuery(id+"F8.wireOp",EDGE,"E4.left"),sQuery(id+"F8.wireOp",EDGE,"E4.right"),sQuery(id+"F8.wireOp",EDGE,"E5.bottom"),sQuery(id+"F8.wireOp",EDGE,"E5.top"),sQuery(id+"F8.wireOp",EDGE,"E5.left"),sQuery(id+"F8.wireOp",EDGE,"E5.right")])],"isStart":false}),makeQuery(id+"F12.opExtrude","CAP_FACE",FACE,{"disambiguationData":[OSD([sQuery(id+"F10.wireOp",EDGE,"E6"),sQuery(id+"F10.wireOp",EDGE,"E7"),sQuery(id+"F10.wireOp",EDGE,"E8"),sQuery(id+"F10.wireOp",EDGE,"E9"),sQuery(id+"F10.wireOp",EDGE,"E10")])],"isStart":false}),makeQuery(id+"F12.opExtrude","CAP_FACE",FACE,{"disambiguationData":[OSD([sQuery(id+"F10.wireOp",EDGE,"E11"),sQuery(id+"F10.wireOp",EDGE,"E12"),sQuery(id+"F10.wireOp",EDGE,"E13"),sQuery(id+"F10.wireOp",EDGE,"E14"),sQuery(id+"F10.wireOp",EDGE,"E25")])],"isStart":false}),makeQuery(id+"F12.opExtrude","SWEPT_FACE",FACE,{"disambiguationData":[OSD([subQ0])]}),makeQuery(id+"F12.opExtrude","CAP_FACE",FACE,{"disambiguationData":[OSD([subQ0,sQuery(id+"F10.wireOp",EDGE,"E16"),sQuery(id+"F10.wireOp",EDGE,"E17"),sQuery(id+"F10.wireOp",EDGE,"E18"),sQuery(id+"F10.wireOp",EDGE,"E19")])],"isStart":false}),makeQuery(id+"F12.opExtrude","CAP_FACE",FACE,{"disambiguationData":[OSD([sQuery(id+"F10.wireOp",EDGE,"E20"),sQuery(id+"F10.wireOp",EDGE,"E21"),sQuery(id+"F10.wireOp",EDGE,"E22"),sQuery(id+"F10.wireOp",EDGE,"E23"),sQuery(id+"F10.wireOp",EDGE,"E24")])],"isStart":false})])],"derivedFrom":makeQuery(id+"F12.opExtrude","CAP_EDGE",EDGE,{"disambiguationData":[OSD([subQ0])],"isStart":false})});}
            fillet(context, id + "F24", {"entities" : qUnion([Q0, Q1, Q2, Q3, Q4, Q5, Q6, Q7, Q8, Q9, Q10, Q11, Q12, Q13, Q14]), "radius" : 1 * mm, "tangentPropagation" : true, "allowEdgeOverflow" : false});
        }
        {
            var Q0;
            Q0=makeQuery(id+"F21.opChamfer","BLEND_EDGE",EDGE,{"blendedFrom":[makeQuery(id+"F5.opExtrude","CAP_EDGE",EDGE,{"disambiguationData":[OSD([sQuery(id+"F4.wireOp",EDGE,"E1.left")])],"isStart":false}),makeQuery(id+"F5.opExtrude","SWEPT_FACE",FACE,{"disambiguationData":[OSD([sQuery(id+"F4.wireOp",EDGE,"E1.right")])]})],"blendedInto":[makeQuery(id+"F5.opExtrude","SWEPT_FACE",FACE,{"disambiguationData":[OSD([sQuery(id+"F4.wireOp",EDGE,"E1.right")])]})]});
            var Q1;
            Q1=makeQuery(id+"F21.opChamfer","BLEND_EDGE",EDGE,{"blendedFrom":[makeQuery(id+"F7.opExtrude","CAP_EDGE",EDGE,{"disambiguationData":[OSD([sQuery(id+"F6.wireOp",EDGE,"E2.right")])],"isStart":false}),makeQuery(id+"F7.opExtrude","SWEPT_FACE",FACE,{"disambiguationData":[OSD([sQuery(id+"F6.wireOp",EDGE,"E2.left")])]})],"blendedInto":[makeQuery(id+"F7.opExtrude","SWEPT_FACE",FACE,{"disambiguationData":[OSD([sQuery(id+"F6.wireOp",EDGE,"E2.left")])]})]});
            var Q2;
            Q2=makeQuery(id+"F21.opChamfer","BLEND_EDGE",EDGE,{"blendedFrom":[makeQuery(id+"F7.opExtrude","CAP_EDGE",EDGE,{"disambiguationData":[OSD([sQuery(id+"F6.wireOp",EDGE,"E3.right")])],"isStart":false}),makeQuery(id+"F7.opExtrude","SWEPT_FACE",FACE,{"disambiguationData":[OSD([sQuery(id+"F6.wireOp",EDGE,"E3.left")])]})],"blendedInto":[makeQuery(id+"F7.opExtrude","SWEPT_FACE",FACE,{"disambiguationData":[OSD([sQuery(id+"F6.wireOp",EDGE,"E3.left")])]})]});
            fillet(context, id + "F25", {"entities" : qUnion([Q0, Q1, Q2]), "radius" : 1 * mm, "tangentPropagation" : true, "allowEdgeOverflow" : false});
        }
    });
